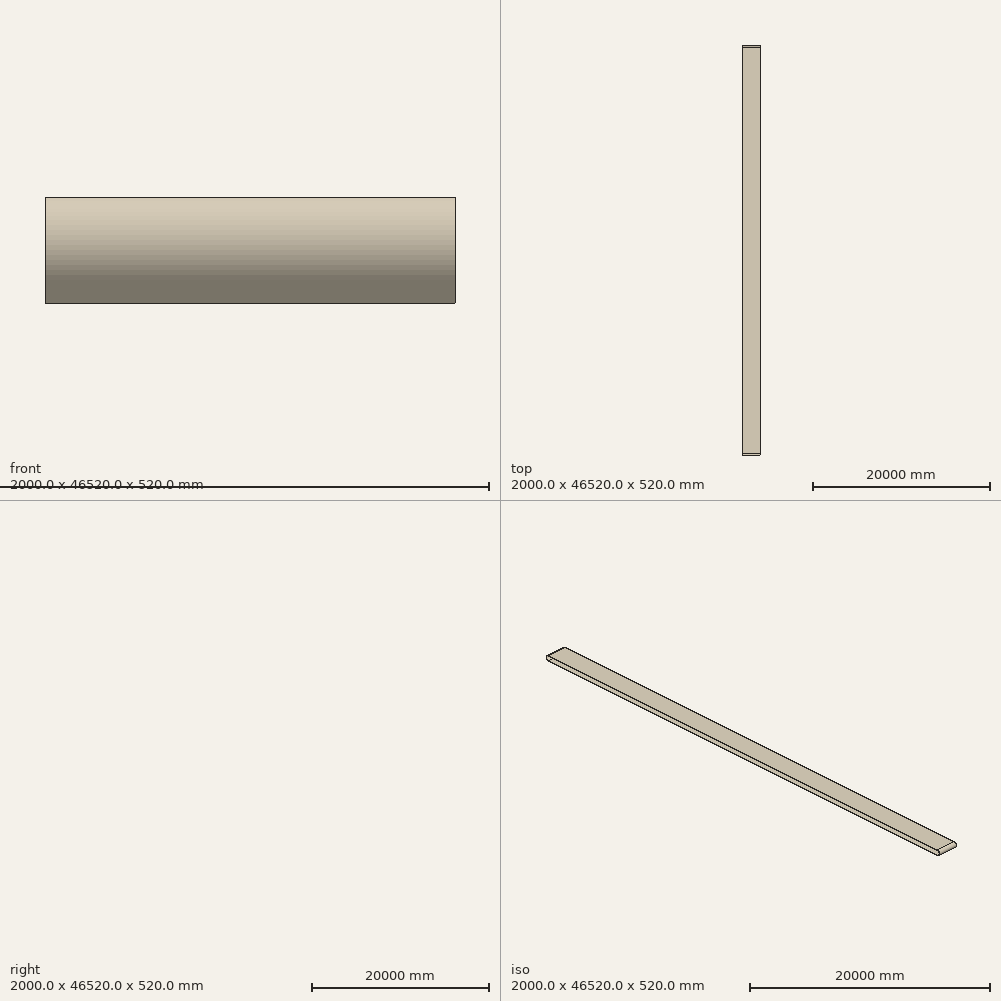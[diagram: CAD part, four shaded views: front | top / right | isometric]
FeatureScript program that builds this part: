
annotation { "Feature Type Name" : "Feature", "Feature Type Description" : "" }
export const myFeature = defineFeature(function(context is Context, id is Id, definition is map)
    precondition{}
    {
        {
            var Q0;
            Q0=qCreatedBy(makeId("Right.planeOp"),FACE);
            var sketch = newSketch(context, id + "F0", { "sketchPlane" : qUnion([Q0])});
            skLineSegment(sketch, "E0.bottom", {"start": v(-20184.26, -4554.44) * mm, "end": v(25815.74, -4554.44) * mm});
            skLineSegment(sketch, "E0.top", {"start": v(-20184.26, -5054.44) * mm, "end": v(25815.74, -5054.44) * mm});
            skLineSegment(sketch, "E0.left", {"start": v(-20184.26, -4554.44) * mm, "end": v(-20184.26, -5054.44) * mm, "construction": true});
            skLineSegment(sketch, "E0.right", {"start": v(25815.74, -4554.44) * mm, "end": v(25815.74, -5054.44) * mm, "construction": true});
            skArc(sketch, "E1", {"start": v(-20184.26, -4554.44) * mm, "mid": v(-20434.26, -4804.44) * mm, "end": v(-20184.26, -5054.44) * mm});
            skArc(sketch, "E2", {"start": v(25815.74, -4554.44) * mm, "mid": v(26065.74, -4804.44) * mm, "end": v(25815.74, -5054.44) * mm});
            skLineSegment(sketch, "E3.0", {"start": v(-20184.26, -5064.44) * mm, "end": v(25815.74, -5064.44) * mm});
            skArc(sketch, "E3.1", {"start": v(-20184.26, -4544.44) * mm, "mid": v(-20444.26, -4804.44) * mm, "end": v(-20184.26, -5064.44) * mm});
            skLineSegment(sketch, "E3.2", {"start": v(-20184.26, -4544.44) * mm, "end": v(25815.74, -4544.44) * mm});
            skArc(sketch, "E3.3", {"start": v(25815.74, -4544.44) * mm, "mid": v(26075.74, -4804.44) * mm, "end": v(25815.74, -5064.44) * mm});
            skSolve(sketch);
        }
        {
            var Q0;
            Q0=makeQuery(id+"F0.imprint","IMPRINT",FACE,{"disambiguationData":[TD([[makeQuery(id+"F0.imprint","IMPRINT",EDGE,{"derivedFrom":sQuery(id+"F0.wireOp",EDGE,"E0.bottom")}),1.0]])]});
            extrude(context, id + "F1", {"entities" : qUnion([Q0]), "depth" : 2000 * mm});
        }
    });
